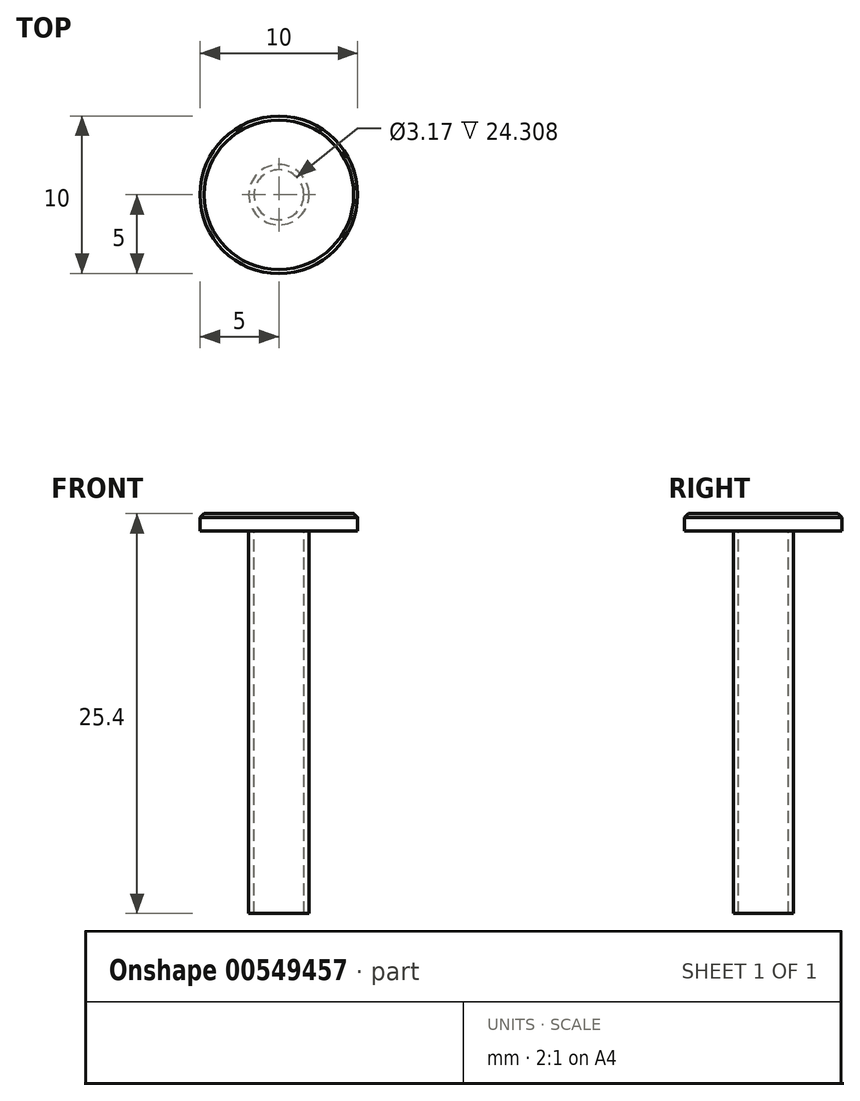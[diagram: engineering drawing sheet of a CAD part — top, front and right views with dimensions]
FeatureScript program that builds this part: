
annotation { "Feature Type Name" : "Feature", "Feature Type Description" : "" }
export const myFeature = defineFeature(function(context is Context, id is Id, definition is map)
    precondition{}
    {
        {
            var Q0;
            Q0=qCreatedBy(makeId("Top.planeOp"),FACE);
            var sketch = newSketch(context, id + "F0", { "sketchPlane" : qUnion([Q0])});
            skCircle(sketch, "E0", {"center": v(0, 0) * mm, "radius": 5 * mm});
            skCircle(sketch, "E1", {"center": v(0, 0) * mm, "radius": 1.91 * mm});
            skSolve(sketch);
        }
        {
            var Q0;
            Q0 = qSketchRegion(id + "F0", true);
            var Q1;
            Q1=makeQuery(id+"F0.imprint","IMPRINT",FACE,{"disambiguationData":[TD([[makeQuery(id+"F0.imprint","IMPRINT",EDGE,{"derivedFrom":sQuery(id+"F0.wireOp",EDGE,"E1")}),1.0]])]});
            extrude(context, id + "F1", {"entities" : qUnion([Q0, Q1]), "depth" : 1.6 * mm, "offsetDistance" : 25.4 * mm});
        }
        {
            var Q0;
            Q0 = qSketchRegion(id + "F0", true);
            var Q1;
            Q1=makeQuery(id+"F1.opExtrude","CAP_FACE",FACE,{"disambiguationData":[OSD([sQuery(id+"F0.wireOp",EDGE,"E0")])],"isStart":false});
            extrude(context, id + "F2", {"entities" : qUnion([Q0, Q1]), "operationType" : NewBodyOperationType.REMOVE, "oppositeDirection" : true, "depth" : 0.5 * mm, "offsetDistance" : 25.4 * mm});
        }
        {
            var Q0;
            Q0=makeQuery(id+"F2.boolean.opBoolean","COPY",FACE,{"derivedFrom":makeQuery(id+"F2.opExtrude","CAP_FACE",FACE,{"disambiguationData":[OSD([sQuery(id+"F0.wireOp",EDGE,"E0")])],"isStart":false})});
            chamfer(context, id + "F3", {"entities" : qUnion([Q0]), "width" : 0.25 * mm, "tangentPropagation" : true});
        }
        {
            var Q0;
            Q0=makeQuery(id+"F2.boolean.opBoolean","COPY",FACE,{"derivedFrom":makeQuery(id+"F2.opExtrude","CAP_FACE",FACE,{"disambiguationData":[OSD([sQuery(id+"F0.wireOp",EDGE,"E0")])],"isStart":false})});
            var sketch = newSketch(context, id + "F4", { "sketchPlane" : qUnion([Q0])});
            skCircle(sketch, "E2.0", {"center": v(0, 0) * mm, "radius": 1.91 * mm});
            skCircle(sketch, "E3", {"center": v(0, 0) * mm, "radius": 1.58 * mm});
            skSolve(sketch);
        }
        {
            var Q0;
            Q0 = qSketchRegion(id + "F4", true);
            extrude(context, id + "F5", {"entities" : qUnion([Q0]), "operationType" : NewBodyOperationType.ADD, "oppositeDirection" : true, "depth" : 25.4 * mm, "offsetDistance" : 25.4 * mm});
        }
    });
